annotation { "Feature Type Name" : "Feature", "Feature Type Description" : "" }
export const myFeature = defineFeature(function(context is Context, id is Id, definition is map)
    precondition{}
    {
        {
            var Q0;
            Q0=qCreatedBy(makeId("Front.planeOp"),FACE);
            var sketch = newSketch(context, id + "F0", { "sketchPlane" : qUnion([Q0])});
            skPoint(sketch, "E0.orphan", {"position": v(0, -3.82) * mm});
            skPoint(sketch, "E1.start.orphan", {"position": v(0, -5) * mm});
            skLineSegment(sketch, "E2", {"start": v(0, -3.82) * mm, "end": v(0, -5) * mm});
            skPoint(sketch, "E3.visualSharp", {"position": v(-43.9, -20.26) * mm});
            skLineSegment(sketch, "E4", {"start": v(-43.9, -20.26) * mm, "end": v(0, -20.26) * mm});
            skLineSegment(sketch, "E5", {"start": v(-43.9, -20.26) * mm, "end": v(-45.9, -20.26) * mm});
            skLineSegment(sketch, "E6", {"start": v(-45.9, -20.26) * mm, "end": v(-45.9, 9.74) * mm});
            skLineSegment(sketch, "E7", {"start": v(-45.9, 9.74) * mm, "end": v(-43.9, 9.74) * mm});
            skLineSegment(sketch, "E8", {"start": v(-43.9, 9.74) * mm, "end": v(-43.9, -18.26) * mm});
            skLineSegment(sketch, "E9", {"start": v(-43.9, -18.26) * mm, "end": v(0, -18.26) * mm});
            skLineSegment(sketch, "E10", {"start": v(0, -18.26) * mm, "end": v(0, -20.26) * mm});
            skSolve(sketch);
        }
        {
            var Q0;
            Q0=makeQuery(id+"F0.imprint","IMPRINT",FACE,{"disambiguationData":[TD([[makeQuery(id+"F0.imprint","IMPRINT",EDGE,{"derivedFrom":sQuery(id+"F0.wireOp",EDGE,"E4")}),1.0]])]});
            var Q1;
            Q1=sQuery(id+"F0.wireOp",EDGE,"E2");
            revolve(context, id + "F1", {"surfaceOperationType" : NewSurfaceOperationType.NEW, "entities" : qUnion([Q0]), "axis" : qUnion([Q1]), "revolveType" : RevolveType.FULL});
        }
        {
            var Q0;
            Q0=makeQuery(id+"F1.opRevolve","SWEPT_FACE",FACE,{"disambiguationData":[OSD([sQuery(id+"F0.wireOp",EDGE,"E4"),sQuery(id+"F0.wireOp",EDGE,"E5")])]});
            var sketch = newSketch(context, id + "F2", { "sketchPlane" : qUnion([Q0])});
            skLineSegment(sketch, "E11", {"start": v(0, 0) * mm, "end": v(0, -20.5) * mm});
            skLineSegment(sketch, "E12.bottom", {"start": v(26.5, -34) * mm, "end": v(-26.5, -34) * mm});
            skLineSegment(sketch, "E12.top", {"start": v(26.5, -7) * mm, "end": v(-26.5, -7) * mm});
            skLineSegment(sketch, "E12.left", {"start": v(28.5, -32) * mm, "end": v(28.5, -9) * mm});
            skLineSegment(sketch, "E12.right", {"start": v(-28.5, -32) * mm, "end": v(-28.5, -9) * mm});
            skPoint(sketch, "E12.middle", {"position": v(0, -20.5) * mm});
            skPoint(sketch, "E13.visualSharp", {"position": v(-28.5, -7) * mm});
            skArc(sketch, "E13.filletArc", {"start": v(-26.5, -7) * mm, "mid": v(-27.91, -7.59) * mm, "end": v(-28.5, -9) * mm});
            skPoint(sketch, "E14.visualSharp", {"position": v(28.5, -7) * mm});
            skArc(sketch, "E14.filletArc", {"start": v(28.5, -9) * mm, "mid": v(27.91, -7.59) * mm, "end": v(26.5, -7) * mm});
            skPoint(sketch, "E15.visualSharp", {"position": v(28.5, -34) * mm});
            skArc(sketch, "E15.filletArc", {"start": v(26.5, -34) * mm, "mid": v(27.91, -33.41) * mm, "end": v(28.5, -32) * mm});
            skPoint(sketch, "E16.visualSharp", {"position": v(-28.5, -34) * mm});
            skArc(sketch, "E16.filletArc", {"start": v(-28.5, -32) * mm, "mid": v(-27.91, -33.41) * mm, "end": v(-26.5, -34) * mm});
            skSolve(sketch);
        }
        {
            var Q0;
            Q0=makeQuery(id+"F2.imprint","IMPRINT",FACE,{"disambiguationData":[TD([[makeQuery(id+"F2.imprint","IMPRINT",EDGE,{"derivedFrom":sQuery(id+"F2.wireOp",EDGE,"E12.bottom")}),-1.0]])]});
            extrude(context, id + "F3", {"entities" : qUnion([Q0]), "operationType" : NewBodyOperationType.REMOVE, "oppositeDirection" : true, "depth" : 25 * mm, "offsetDistance" : 25 * mm});
        }
        {
            var Q0;
            Q0=makeQuery(id+"F1.opRevolve","SWEPT_FACE",FACE,{"disambiguationData":[OSD([sQuery(id+"F0.wireOp",EDGE,"E4"),sQuery(id+"F0.wireOp",EDGE,"E5")])]});
            var sketch = newSketch(context, id + "F4", { "sketchPlane" : qUnion([Q0])});
            skText(sketch, "E17", { "text": "FLAT COVER\nTS APO 56Q", "fontName": "AllertaStencil-Regular.ttf"});
            skLineSegment(sketch, "E18", {"start": v(0, 0) * mm, "end": v(0.2, 14.38) * mm, "construction": true});
            const initialGuessF4  = {"E17": [-0.02886, 0.00762, 1, 0, 0.00676]};
            skSetInitialGuess(sketch, initialGuessF4);
            skSolve(sketch);
        }
        {
            var Q0;
            Q0 = qSketchRegion(id + "F4", true);
            extrude(context, id + "F5", {"entities" : qUnion([Q0]), "operationType" : NewBodyOperationType.REMOVE, "oppositeDirection" : true, "depth" : 2 * mm, "offsetDistance" : 25 * mm});
        }
    });